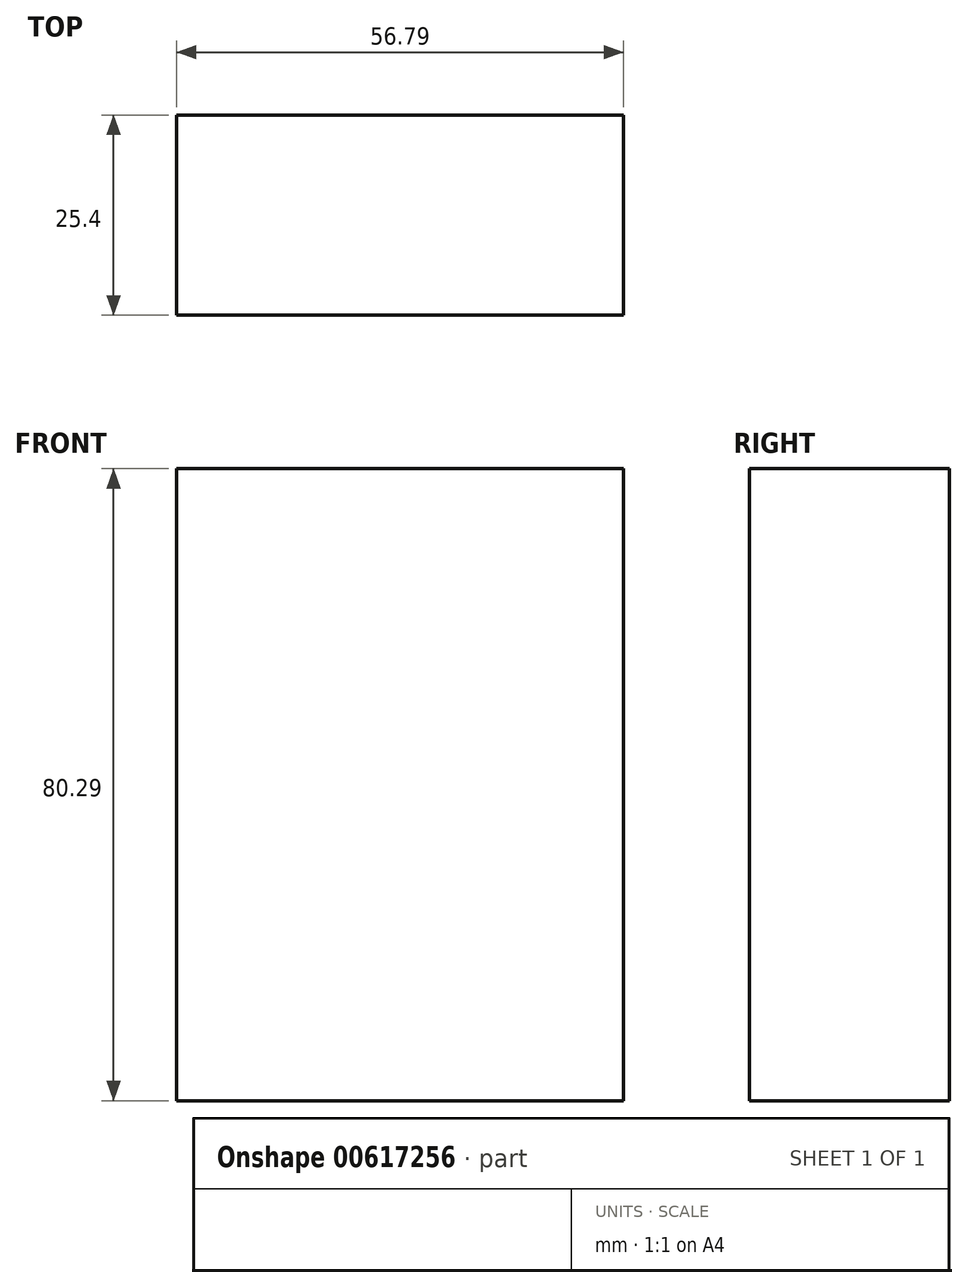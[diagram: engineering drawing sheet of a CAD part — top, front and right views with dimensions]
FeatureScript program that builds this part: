
annotation { "Feature Type Name" : "Feature", "Feature Type Description" : "" }
export const myFeature = defineFeature(function(context is Context, id is Id, definition is map)
    precondition{}
    {
        {
            var Q0;
            Q0=qCreatedBy(makeId("Front.planeOp"),FACE);
            var sketch = newSketch(context, id + "F0", { "sketchPlane" : qUnion([Q0])});
            skLineSegment(sketch, "E0", {"start": v(-31.47, 47.98) * mm, "end": v(-31.47, -32.31) * mm});
            skLineSegment(sketch, "E1", {"start": v(-31.47, 47.98) * mm, "end": v(25.32, 47.98) * mm});
            skLineSegment(sketch, "E2", {"start": v(25.32, 47.98) * mm, "end": v(25.32, -32.31) * mm});
            skLineSegment(sketch, "E3", {"start": v(25.32, -32.31) * mm, "end": v(-31.47, -32.31) * mm});
            skSolve(sketch);
        }
        {
            var Q0;
            Q0=makeQuery(id+"F0.imprint","IMPRINT",FACE,{"disambiguationData":[TD([[makeQuery(id+"F0.imprint","IMPRINT",EDGE,{"derivedFrom":sQuery(id+"F0.wireOp",EDGE,"E0")}),1.0]])]});
            extrude(context, id + "F1", {"entities" : qUnion([Q0]), "depth" : 25.4 * mm, "offsetDistance" : 25.4 * mm});
        }
    });
